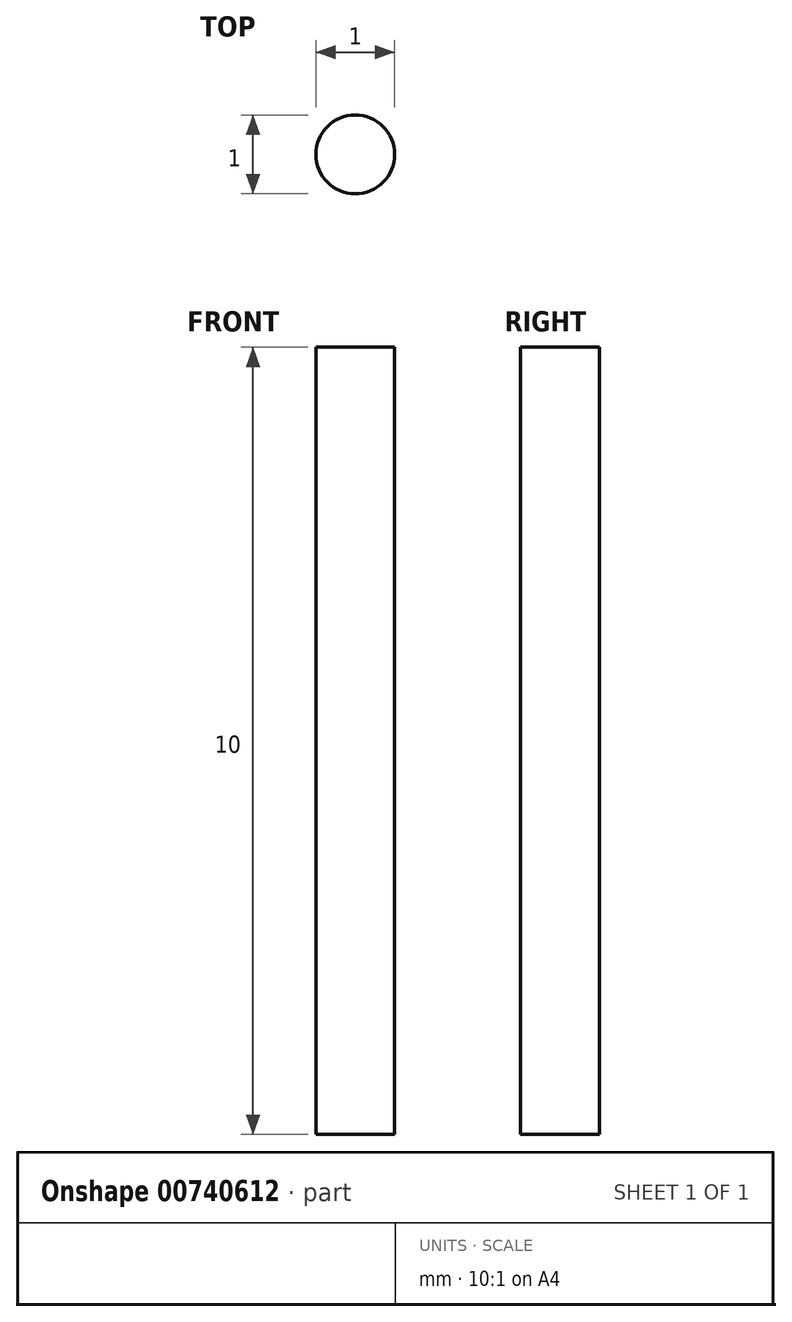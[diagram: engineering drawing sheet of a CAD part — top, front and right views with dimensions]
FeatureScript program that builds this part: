
annotation { "Feature Type Name" : "Feature", "Feature Type Description" : "" }
export const myFeature = defineFeature(function(context is Context, id is Id, definition is map)
    precondition{}
    {
        {
            var Q0;
            Q0=qCreatedBy(makeId("Top.planeOp"),FACE);
            var sketch = newSketch(context, id + "F0", { "sketchPlane" : qUnion([Q0])});
            skCircle(sketch, "E0", {"center": v(0, 0) * mm, "radius": 0.5 * mm});
            skSolve(sketch);
        }
        {
            var Q0;
            Q0=makeQuery(id+"F0.imprint","IMPRINT",FACE,{"disambiguationData":[TD([[makeQuery(id+"F0.imprint","IMPRINT",EDGE,{"derivedFrom":sQuery(id+"F0.wireOp",EDGE,"E0")}),1.0]])]});
            extrude(context, id + "F1", {"entities" : qUnion([Q0]), "depth" : 10 * mm, "offsetDistance" : 25 * mm});
        }
    });
